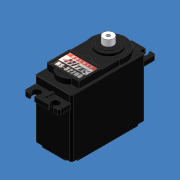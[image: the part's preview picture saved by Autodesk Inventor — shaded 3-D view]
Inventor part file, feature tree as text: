
AUTODESK INVENTOR PART (.ipt)
format: ipt  version: 2012 (Build 160160000, 160)  size: 722,944 bytes
history: native  units: mm (DEFAULTED — no unit token found)
features: sketch x13, extrude x11, fillet x5, mirror x4, chamfer x2, plane x1, hole x1, projected_geometry x1, other x1
ambient origin geometry x8: Origin, YZ Plane, XZ Plane, XY Plane, X Axis, Y Axis, Z Axis, Center Point
bodies: Solid1 (feature_tree)
feature tree (39):
  extrude  "Extrusion1"  Depth=20.0mm
  extrude  "Extrusion2"  Depth=17.75mm
  extrude  "Extrusion3"  Depth=18.6mm
  extrude  "Extrusion4"  Depth=3.0mm TaperAngle=0.0deg
  plane  "Work Plane1"
  extrude  "Extrusion5"  Depth=9.0mm
  extrude  "Extrusion6"  Depth=1.5mm TaperAngle=0.0deg
  mirror  "Mirror2"
  extrude  "Extrusion7"  Depth=0.5mm TaperAngle=0.0deg
  mirror  "Mirror3"
  fillet  "Fillet2"  [1 undecoded]
  extrude  "Extrusion8"  Depth=6.4mm
  hole  "Hole1"  [1 undecoded]
  mirror  "Mirror4"
  mirror  "Mirror5"
  fillet  "Fillet4"  Radius=5.1mm
  chamfer  "Chamfer1"  Distance=2.5mm
  fillet  "Fillet5"  Radius=1.16mm
  chamfer  "Chamfer2"  Distance=0.9mm
  extrude  "Extrusion9"  Depth=1.0mm
  fillet  "Fillet6"  Radius=4.0mm
  extrude  "Extrusion10"  Depth=1.5mm TaperAngle=0.0deg
  fillet  "Fillet7"  Radius=2.0mm
  extrude  "Extrusion11"  Depth=0.25mm
  sketch  "Sketch1"  dims[d0=40.0mm d1=20.0mm]
  sketch  "Sketch2"  dims[d2=33.0mm d3=0.0mm d4=17.75mm]
  sketch  "Sketch3"  dims[d5=5.0mm d6=18.6mm]
  sketch  "Sketch4"  dims[d7=10.0mm d8=3.0mm d9=0.0mm]
  sketch  "Sketch5"  dims[d11=4.0mm d12=9.0mm]
  projected_geometry  "Projected Loop1"
  sketch  "Sketch6"  dims[d13=12.9mm d14=1.5mm d15=0.0mm]
  sketch  "Sketch7"  dims[d16=9.95mm d17=0.5mm d18=0.0mm d19=-26.5mm]
  sketch  "Sketch8"  dims[d20=18.9mm d21=6.4mm]
  sketch  "Sketch9"  dims[d22=2.5mm d23=0.0mm d26=3.9mm d27=5.1mm]
  sketch  "Sketch10"  dims[d28=4.4mm]
  sketch  "Sketch11"  dims[d29=2.6mm d30=2.5mm d31=0.0mm d33=1.16mm]
  sketch  "Sketch12"  dims[d34=4.0mm]
  sketch  "Sketch13"  dims[d35=0.58mm d36=0.9mm d37=0.0mm d38=1.0mm d39=4.0mm d40=1.5mm d41=0.0mm d43=2.0mm d44=0.25mm d45=2.0mm d46=1.0mm d47=0.75mm d48=2.0mm d49=5.7mm d50=3.4mm d51=0.0mm d52=2.0mm d53=0.5mm d54=12.85mm d55=4.0mm d56=0.5mm d57=0.0mm d58=0.5mm d59=1.0mm d60=1.0mm d61=1.0mm d62=0.5mm d63=0.0mm d64=2.0mm d65=2.0mm d66=1.8mm d67=6.0mm d68=4.0mm d69=2.0mm d70=14.3117mm d71=8.0mm d72=20.594885mm d76=45.0deg d77=45.0deg]
  other  "Image1"
note: 2 required parameter values undecoded (feature->parameter linkage not recoverable at this tier; creation-order binding heuristic only, values carry confidence <= 0.55)
